# Revit family: EKF_EE_ЦокольВРУUNIT_PROxima
name_source: partatom
category: Электрооборудование
units: mm (PartAtom-declared; Revit-internal decimal feet)

## family parameters
Всегда вертикально = Нет
На основе рабочей плоскости = Да
Общий = Да
При загрузке вырезать с полостями = Нет
Размер круглого соединителя = Использовать диаметр
Тип детали = Силовой щит
Точка расчета площади = Нет

## types (5) — shared parameters
ADSK_Единица измерения = шт.
ADSK_Завод-изготовитель = EKF
ADSK_Количество = 1
ADSK_Марка = Цоколь
ADSK_Материал = RAL 7035_Сталь
ADSK_Обозначение = Цоколь
ADSK_Размер_Высота = 100 мм
D = 9 мм
t = 1 мм
Изготовитель = EKF
Отметка по умолчанию = 1219.2 мм
Отступ = 20 мм
Серия номенклатуры = Unit PROxima
Степень защиты IP = -
ТВ = EKF_2
Тип установки = -
zero-valued in all types: ADSK_Масса

## per-type parameters (varying)
| type | ADSK_Код изделия | ADSK_Размер_Глубина | ADSK_Размер_Ширина | Тип |
| Цоколь к ВРУ Unit S IP31 (Вх450х450) EKF PROxima | mb15-08-02-03 | 450 мм | 450 мм | 77 мм |
| Цоколь к ВРУ Unit S IP31 (Вх600х450) EKF PROxima | mb15-08-02-04 | 450 мм | 600 мм | 78 мм |
| Цоколь к ВРУ Unit S IP31 (Вх600х600) EKF PROxima | mb15-08-02-06 | 600 мм | 600 мм | 79 мм |
| Цоколь к ВРУ Unit S IP31 (Вх800х450) EKF PROxima | mb15-08-02-05 | 450 мм | 800 мм | 80 мм |
| Цоколь к ВРУ Unit S IP31 (Вх800х600) EKF PROxima | mb15-08-02-07 | 600 мм | 800 мм | 81 мм |

note: column(s) folded — value = type name in every type: ADSK_Наименование
